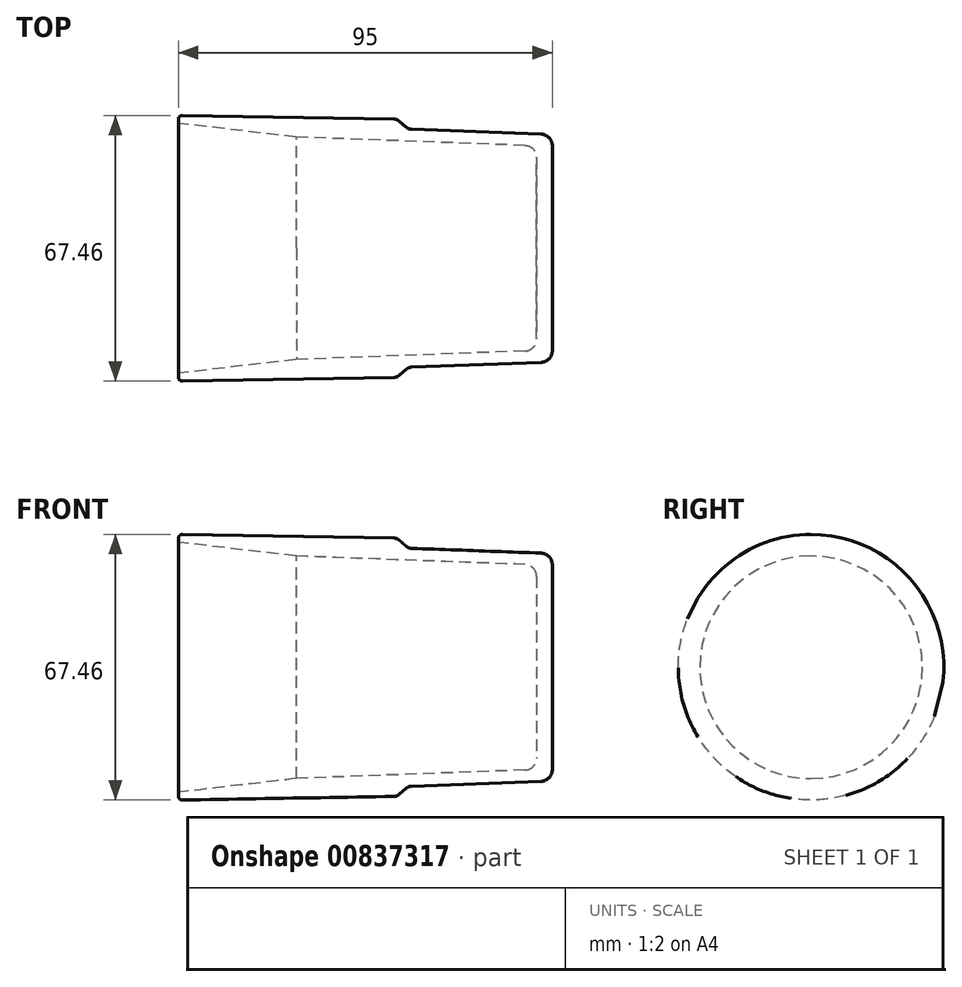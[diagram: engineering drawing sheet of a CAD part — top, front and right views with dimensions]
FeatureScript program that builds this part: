
annotation { "Feature Type Name" : "Feature", "Feature Type Description" : "" }
export const myFeature = defineFeature(function(context is Context, id is Id, definition is map)
    precondition{}
    {
        {
            var Q0;
            Q0=qCreatedBy(makeId("Top.planeOp"),FACE);
            var sketch = newSketch(context, id + "F0", { "sketchPlane" : qUnion([Q0])});
            skLineSegment(sketch, "E0", {"start": v(0, 0) * mm, "end": v(-150.06, 0) * mm, "construction": true});
            skLineSegment(sketch, "E1", {"start": v(0, 0) * mm, "end": v(0, 28.9) * mm});
            skLineSegment(sketch, "E2", {"start": v(0, 28.9) * mm, "end": v(-36.5, 30.25) * mm});
            skLineSegment(sketch, "E3", {"start": v(-36.5, 30.25) * mm, "end": v(-39.5, 32.8) * mm});
            skLineSegment(sketch, "E4", {"start": v(-39.5, 32.8) * mm, "end": v(-95, 33.75) * mm});
            skLineSegment(sketch, "E5", {"start": v(-95, 33.75) * mm, "end": v(-95, 31.75) * mm});
            skLineSegment(sketch, "E6", {"start": v(-95, 31.75) * mm, "end": v(-65, 28.26) * mm});
            skLineSegment(sketch, "E7", {"start": v(-65, 28.26) * mm, "end": v(-4, 26) * mm});
            skLineSegment(sketch, "E8", {"start": v(-4, 26) * mm, "end": v(-4, 0) * mm});
            skLineSegment(sketch, "E9", {"start": v(-4, 0) * mm, "end": v(0, 0) * mm});
            skLineSegment(sketch, "E10", {"start": v(0, 0) * mm, "end": v(-100.8, 0) * mm, "construction": true});
            skSolve(sketch);
        }
        {
            var Q0;
            Q0=makeQuery(id+"F0.imprint","IMPRINT",FACE,{"disambiguationData":[TD([[makeQuery(id+"F0.imprint","IMPRINT",EDGE,{"derivedFrom":sQuery(id+"F0.wireOp",EDGE,"E1")}),1.0]])]});
            var Q1;
            Q1=sQuery(id+"F0.wireOp",EDGE,"E0");
            revolve(context, id + "F1", {"surfaceOperationType" : NewSurfaceOperationType.NEW, "entities" : qUnion([Q0]), "axis" : qUnion([Q1]), "revolveType" : RevolveType.FULL});
        }
        {
            var Q0;
            Q0=makeQuery(id+"F1.opRevolve","SWEPT_EDGE",EDGE,{"disambiguationData":[OSD([sQuery(id+"F0.wireOp",EDGE,"E4"),sQuery(id+"F0.wireOp",EDGE,"E5")])]});
            fillet(context, id + "F2", {"entities" : qUnion([Q0]), "radius" : 1 * mm, "tangentPropagation" : true, "allowEdgeOverflow" : false});
        }
        {
            var Q0;
            Q0=makeQuery(id+"F1.opRevolve","SWEPT_EDGE",EDGE,{"disambiguationData":[OSD([sQuery(id+"F0.wireOp",EDGE,"E5"),sQuery(id+"F0.wireOp",EDGE,"E6")])]});
            fillet(context, id + "F3", {"entities" : qUnion([Q0]), "radius" : 0.5 * mm, "tangentPropagation" : true, "allowEdgeOverflow" : false});
        }
        {
            var Q0;
            Q0=makeQuery(id+"F1.opRevolve","SWEPT_EDGE",EDGE,{"disambiguationData":[OSD([sQuery(id+"F0.wireOp",EDGE,"E1"),sQuery(id+"F0.wireOp",EDGE,"E2")])]});
            fillet(context, id + "F4", {"entities" : qUnion([Q0]), "radius" : 3 * mm, "tangentPropagation" : true, "allowEdgeOverflow" : false});
        }
        {
            var Q0;
            Q0=makeQuery(id+"F1.opRevolve","SWEPT_EDGE",EDGE,{"disambiguationData":[OSD([sQuery(id+"F0.wireOp",EDGE,"E2"),sQuery(id+"F0.wireOp",EDGE,"E3")])]});
            var Q1;
            Q1=makeQuery(id+"F1.opRevolve","SWEPT_EDGE",EDGE,{"disambiguationData":[OSD([sQuery(id+"F0.wireOp",EDGE,"E3"),sQuery(id+"F0.wireOp",EDGE,"E4")])]});
            fillet(context, id + "F5", {"entities" : qUnion([Q0, Q1]), "radius" : 2 * mm, "tangentPropagation" : true, "allowEdgeOverflow" : false});
        }
        {
            var Q0;
            Q0=makeQuery(id+"F1.opRevolve","SWEPT_EDGE",EDGE,{"disambiguationData":[OSD([sQuery(id+"F0.wireOp",EDGE,"E7"),sQuery(id+"F0.wireOp",EDGE,"E8")])]});
            fillet(context, id + "F6", {"entities" : qUnion([Q0]), "radius" : 3 * mm, "tangentPropagation" : true, "allowEdgeOverflow" : false});
        }
    });
